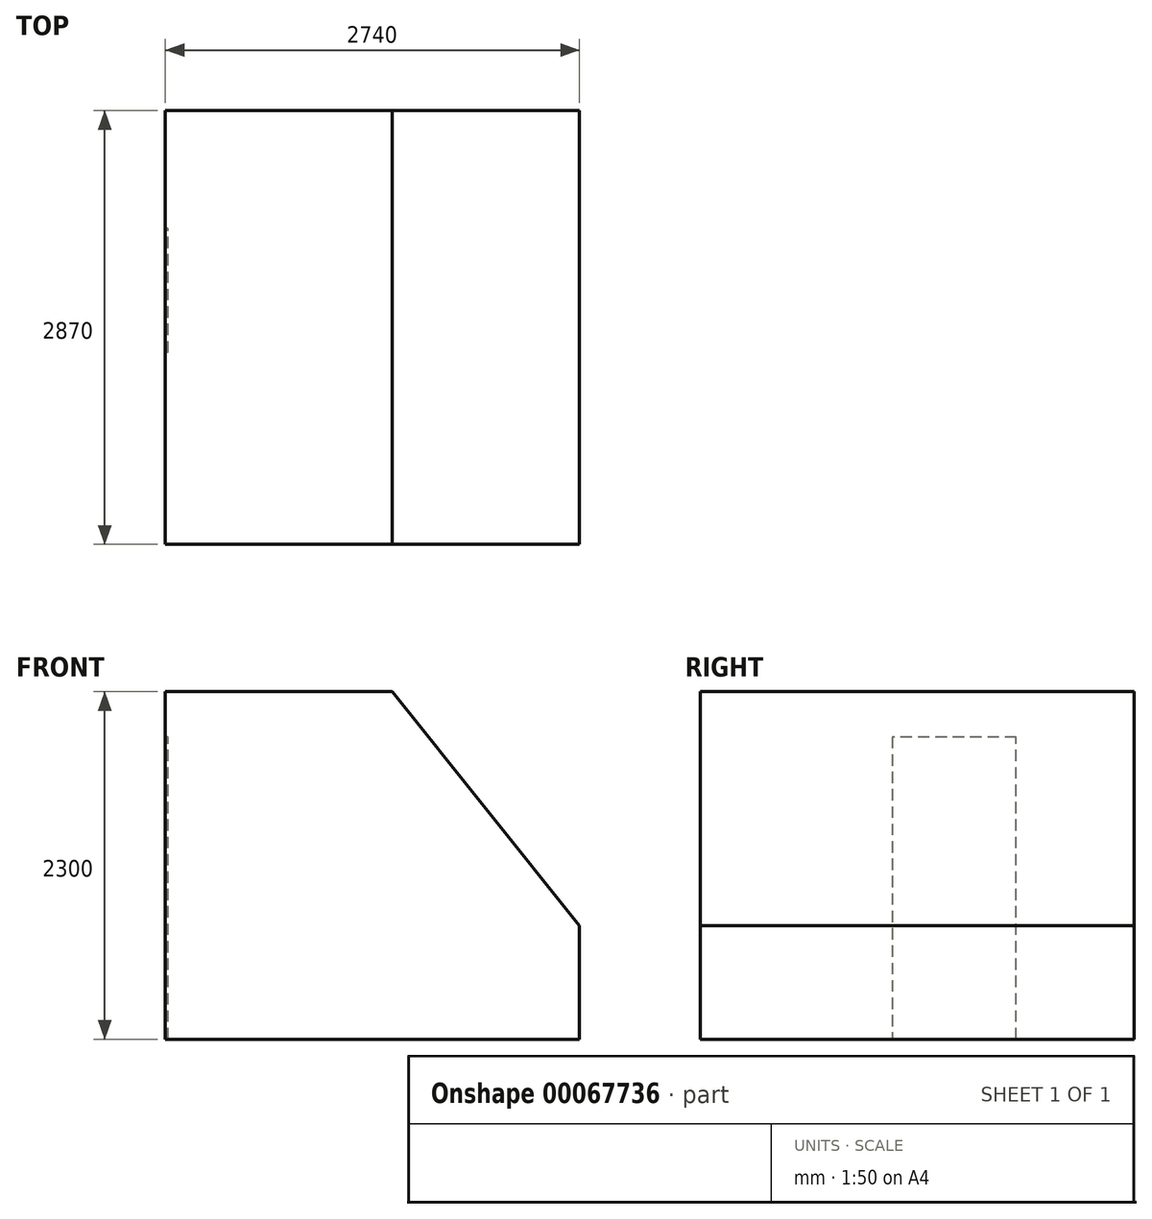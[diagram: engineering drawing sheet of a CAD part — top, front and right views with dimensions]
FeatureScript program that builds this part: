
annotation { "Feature Type Name" : "Feature", "Feature Type Description" : "" }
export const myFeature = defineFeature(function(context is Context, id is Id, definition is map)
    precondition{}
    {
        {
            var Q0;
            Q0=qCreatedBy(makeId("Front.planeOp"),FACE);
            var sketch = newSketch(context, id + "F0", { "sketchPlane" : qUnion([Q0])});
            skLineSegment(sketch, "E0", {"start": v(0, 0) * mm, "end": v(2740, 0) * mm});
            skLineSegment(sketch, "E1", {"start": v(2740, 0) * mm, "end": v(2740, 750) * mm});
            skLineSegment(sketch, "E2", {"start": v(2740, 750) * mm, "end": v(1500, 2300) * mm});
            skLineSegment(sketch, "E3", {"start": v(1500, 2300) * mm, "end": v(0, 2300) * mm});
            skLineSegment(sketch, "E4", {"start": v(0, 2300) * mm, "end": v(0, 0) * mm});
            skSolve(sketch);
        }
        {
            var Q0;
            Q0=makeQuery(id+"F0.imprint","IMPRINT",FACE,{"disambiguationData":[TD([[makeQuery(id+"F0.imprint","IMPRINT",EDGE,{"derivedFrom":sQuery(id+"F0.wireOp",EDGE,"E0")}),1.0]])]});
            extrude(context, id + "F1", {"entities" : qUnion([Q0]), "depth" : 2870 * mm});
        }
        {
            var Q0;
            Q0=makeQuery(id+"F1.opExtrude","SWEPT_FACE",FACE,{"disambiguationData":[OSD([sQuery(id+"F0.wireOp",EDGE,"E4")])]});
            var sketch = newSketch(context, id + "F2", { "sketchPlane" : qUnion([Q0])});
            skLineSegment(sketch, "E5", {"start": v(780, 0) * mm, "end": v(780, 2000) * mm});
            skLineSegment(sketch, "E6", {"start": v(780, 2000) * mm, "end": v(1600, 2000) * mm});
            skLineSegment(sketch, "E7", {"start": v(1600, 2000) * mm, "end": v(1600, 0) * mm});
            skLineSegment(sketch, "E8", {"start": v(1600, 0) * mm, "end": v(780, 0) * mm});
            skSolve(sketch);
        }
        {
            var Q0;
            Q0=makeQuery(id+"F2.imprint","IMPRINT",FACE,{"disambiguationData":[TD([[makeQuery(id+"F2.imprint","IMPRINT",EDGE,{"derivedFrom":sQuery(id+"F2.wireOp",EDGE,"E5")}),-1.0]])]});
            extrude(context, id + "F3", {"entities" : qUnion([Q0]), "operationType" : NewBodyOperationType.REMOVE, "oppositeDirection" : true, "depth" : 20 * mm});
        }
    });
